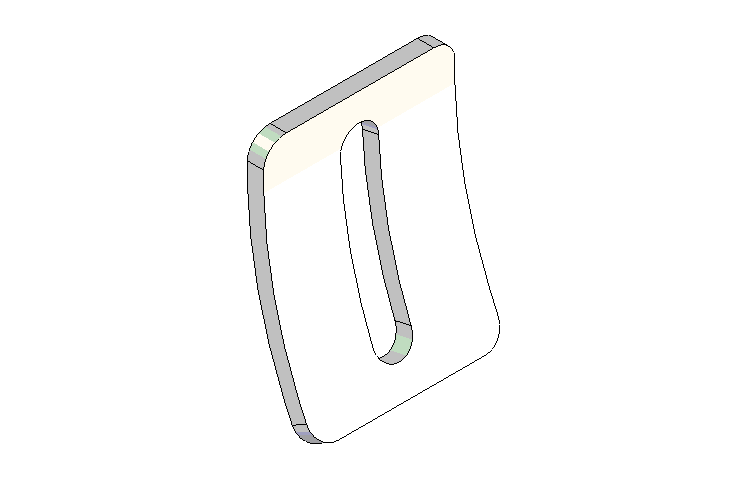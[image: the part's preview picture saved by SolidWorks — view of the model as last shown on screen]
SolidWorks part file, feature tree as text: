
SOLIDWORKS PART (.sldprt)
format: sldprt  version: not decoded by parser v0  size: 222,720 bytes
history: native  units: mm
features: plane x4, sketch x2, material x1, extrude x1, fillet x1, cut_extrude x1 (+10 scaffold rows collapsed)
feature tree (20):
  scaffold x10  (default folders/planes/origin — collapsed)
  material  "Matériau <non spécifié>"
  plane  "Plan de face"
  plane  "Plan de dessus"
  plane  "Plan de droite"
  sketch  "Esquisse1"  dims[c1.D1=~71.549207mm c1.D2=85.0mm c1.D4=85.0mm c2.D1=82.0mm c2.D2=82.0mm c3.D1=3.0mm c3.D3=46.0mm c3.D4=10.0mm c3.D5=82.0mm c4.D1=3.0mm c4.D4=9.5mm c4.D3=44.0mm]
  extrude  "Extrusion1"  Depth=35mm
  fillet  "Congé1"  Radius=4mm
  plane  "Plan1"
  sketch  "Esquisse2"  dims[c1.D2=3.5mm c1.D1=7.0mm c2.D2=35.0mm]
  cut_extrude  "Enlèv. mat.-Extru.1"  Depth=35mm
decode coverage: 5 of 5 modeling features carry decoded parameters
note: ~ marks probable driven/reference dimensions
note: suppression state not decoded; provenance and decode notes live in map.json
